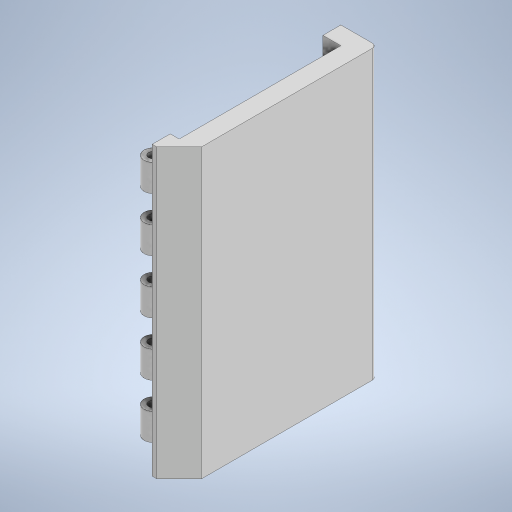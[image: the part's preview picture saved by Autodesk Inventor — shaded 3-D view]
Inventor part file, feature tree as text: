
AUTODESK INVENTOR PART (.ipt)
format: ipt  version: 2023 (Build 270158030, 158C)  size: 276,992 bytes
history: native  units: in
note: dims shown in document units (in); Inventor stores cm internally (conversion verified against a paired STEP export)
features: extrude x6, sketch x6, fillet x1, plane x1, pattern_linear x1, chamfer x1
ambient origin geometry x8: Origin, YZ Plane, XZ Plane, XY Plane, X Axis, Y Axis, Z Axis, Center Point
bodies: Solid1 (feature_tree)
feature tree (16):
  extrude  "Extrusion1"  Depth=6.0in
  extrude  "Extrusion2"  Depth=0.5in
  fillet  "Fillet1"  Radius=0.5in
  extrude  "Extrusion3"  Depth=0.5in
  plane  "Work Plane1"
  extrude  "Extrusion4"  Depth=0.25in
  pattern_linear  "Rectangular Pattern1"  Spacing1=-0.75in  [1 undecoded]
  extrude  "Extrusion5"  Depth=0.5in
  chamfer  "Chamfer2"  Distance=0.25in
  extrude  "Extrusion6"  Depth=0.5in
  sketch  "Sketch1"  dims[d0=8.0in d1=6.0in]
  sketch  "Sketch2"  dims[d2=0.5in d3=0.0in d4=0.5in d5=0.5in d6=0.0in]
  sketch  "Sketch3"  dims[d7=0.125in d8=0.5in]
  sketch  "Sketch4"  dims[d9=0.5in d10=0.25in]
  sketch  "Sketch5"  dims[d11=90.0deg]
  sketch  "Sketch6"  dims[d12=6.625in d13=0.0in d14=-0.75in d15=0.475in d16=0.25in d17=0.5in d18=0.75in d19=0.75in d20=0.75in d21=0.0in d22=1.9685in d24=1.5in d29=8.0in d30=0.0in d31=0.625in d32=0.125in d33=45.0deg d35=2.5in d37=0.25in d38=2.0in d39=0.15in d40=0.0in d28=0.5in]
note: 1 required parameter value undecoded (feature->parameter linkage not recoverable at this tier; creation-order binding heuristic only, values carry confidence <= 0.55)
